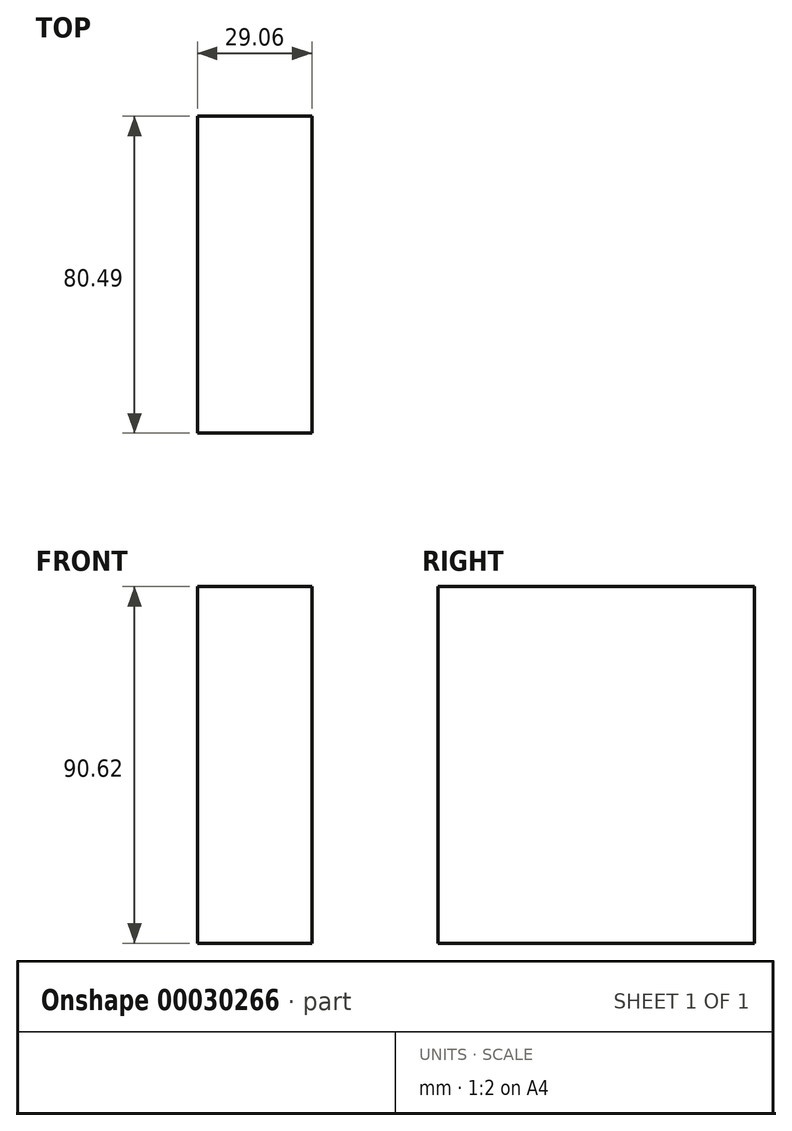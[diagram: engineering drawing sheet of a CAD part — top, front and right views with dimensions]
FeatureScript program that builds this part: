
annotation { "Feature Type Name" : "Feature", "Feature Type Description" : "" }
export const myFeature = defineFeature(function(context is Context, id is Id, definition is map)
    precondition{}
    {
        {
            var Q0;
            Q0=qCreatedBy(makeId("Front.planeOp"),FACE);
            var sketch = newSketch(context, id + "F0", { "sketchPlane" : qUnion([Q0])});
            skLineSegment(sketch, "E0.bottom", {"start": v(-110.42, 45.03) * mm, "end": v(-81.36, 45.03) * mm});
            skLineSegment(sketch, "E0.top", {"start": v(-110.42, -45.6) * mm, "end": v(-81.36, -45.6) * mm});
            skLineSegment(sketch, "E0.left", {"start": v(-110.42, 45.03) * mm, "end": v(-110.42, -45.6) * mm});
            skLineSegment(sketch, "E0.right", {"start": v(-81.36, 45.03) * mm, "end": v(-81.36, -45.6) * mm});
            skSolve(sketch);
        }
        {
            var Q0;
            Q0=makeQuery(id+"F0.imprint","IMPRINT",FACE,{"disambiguationData":[TD([[makeQuery(id+"F0.imprint","IMPRINT",EDGE,{"derivedFrom":sQuery(id+"F0.wireOp",EDGE,"E0.bottom")}),-1.0]])]});
            extrude(context, id + "F1", {"entities" : qUnion([Q0]), "depth" : 80.49 * mm});
        }
    });
